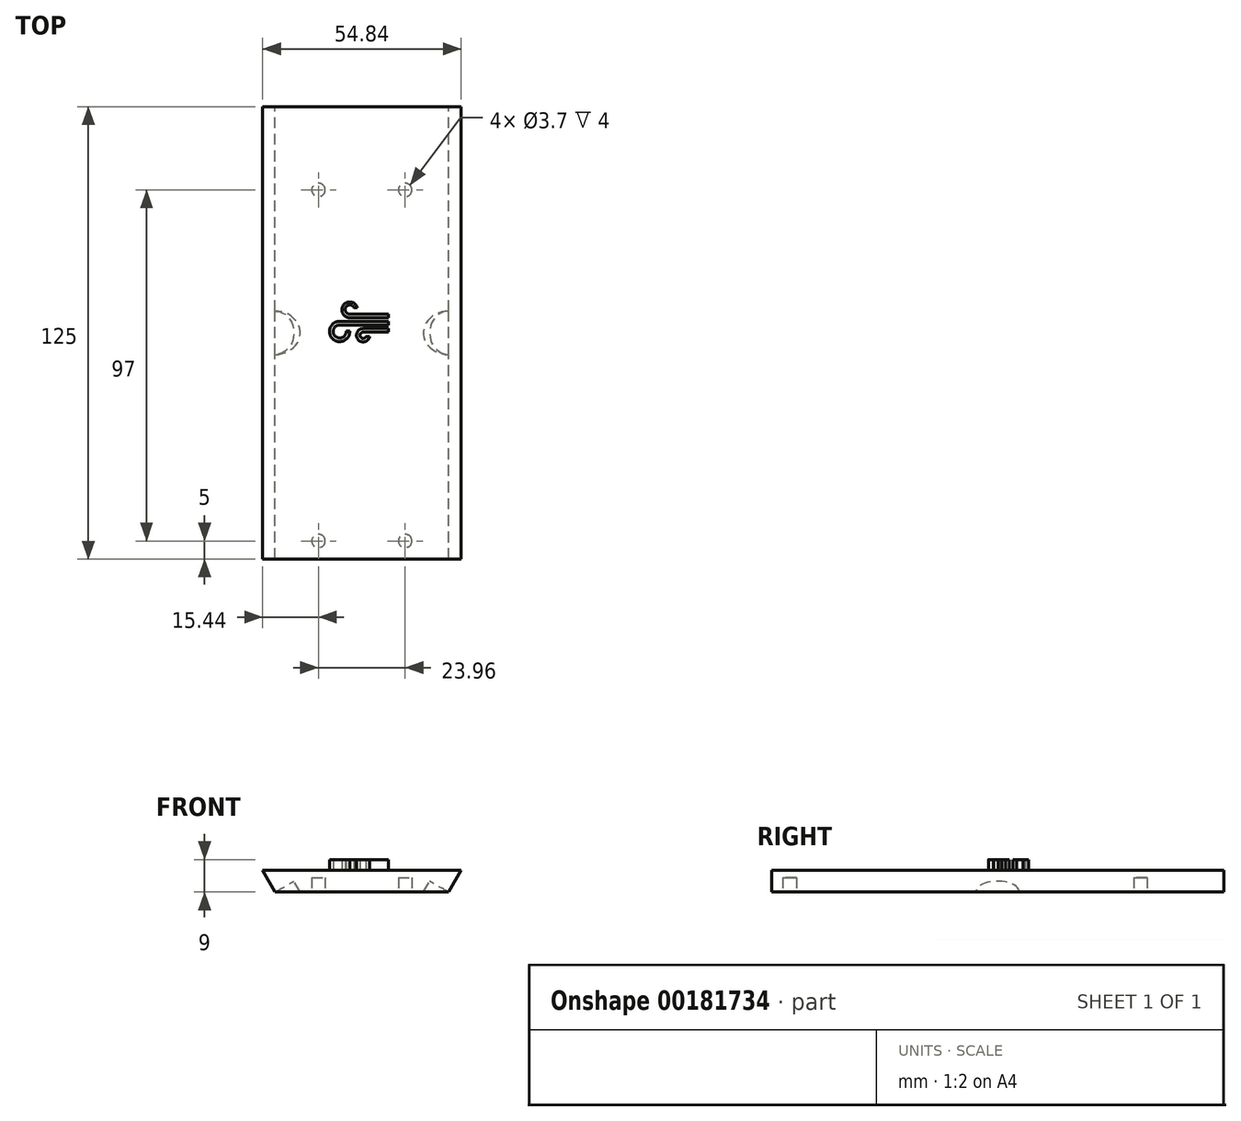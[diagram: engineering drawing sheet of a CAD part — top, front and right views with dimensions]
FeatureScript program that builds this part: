
annotation { "Feature Type Name" : "Feature", "Feature Type Description" : "" }
export const myFeature = defineFeature(function(context is Context, id is Id, definition is map)
    precondition{}
    {
        {
            var Q0;
            Q0=qCreatedBy(makeId("Front.planeOp"),FACE);
            var sketch = newSketch(context, id + "F0", { "sketchPlane" : qUnion([Q0])});
            skCircle(sketch, "E0.cCircle", {"center": v(0, 0) * mm, "radius": 47.5 * mm, "construction": true});
            skLineSegment(sketch, "E0.0", {"start": v(-27.42, -47.5) * mm, "end": v(-54.85, 0) * mm});
            skLineSegment(sketch, "E0.1", {"start": v(-54.85, 0) * mm, "end": v(-27.42, 47.5) * mm});
            skLineSegment(sketch, "E0.2", {"start": v(-27.42, 47.5) * mm, "end": v(27.42, 47.5) * mm});
            skLineSegment(sketch, "E0.3", {"start": v(27.42, 47.5) * mm, "end": v(54.85, 0) * mm});
            skLineSegment(sketch, "E0.4", {"start": v(54.85, 0) * mm, "end": v(27.42, -47.5) * mm});
            skLineSegment(sketch, "E0.5", {"start": v(27.42, -47.5) * mm, "end": v(-27.42, -47.5) * mm});
            skPoint(sketch, "E0.0.midPoint", {"position": v(-41.14, -23.75) * mm});
            skCircle(sketch, "E1.cCircle", {"center": v(0, 0) * mm, "radius": 41.5 * mm, "construction": true});
            skLineSegment(sketch, "E1.0", {"start": v(-23.96, -41.5) * mm, "end": v(-47.92, 0) * mm});
            skLineSegment(sketch, "E1.1", {"start": v(-47.92, 0) * mm, "end": v(-23.96, 41.5) * mm});
            skLineSegment(sketch, "E1.2", {"start": v(-23.96, 41.5) * mm, "end": v(23.96, 41.5) * mm});
            skLineSegment(sketch, "E1.3", {"start": v(23.96, 41.5) * mm, "end": v(47.92, 0) * mm});
            skLineSegment(sketch, "E1.4", {"start": v(47.92, 0) * mm, "end": v(23.96, -41.5) * mm});
            skLineSegment(sketch, "E1.5", {"start": v(23.96, -41.5) * mm, "end": v(-23.96, -41.5) * mm});
            skPoint(sketch, "E1.0.midPoint", {"position": v(-35.94, -20.75) * mm});
            skLineSegment(sketch, "E2", {"start": v(27.42, 47.5) * mm, "end": v(23.96, 41.5) * mm});
            skLineSegment(sketch, "E3", {"start": v(-27.42, 47.5) * mm, "end": v(-23.96, 41.5) * mm});
            skSolve(sketch);
        }
        {
            var Q0;
            Q0=makeQuery(id+"F0.imprint","IMPRINT",FACE,{"disambiguationData":[TD([[makeQuery(id+"F0.imprint","IMPRINT",EDGE,{"derivedFrom":sQuery(id+"F0.wireOp",EDGE,"E0.2")}),-1.0]])]});
            extrude(context, id + "F1", {"entities" : qUnion([Q0]), "depth" : 125 * mm});
        }
        {
            var Q0;
            Q0=makeQuery(id+"F1.opExtrude","SWEPT_FACE",FACE,{"disambiguationData":[OSD([sQuery(id+"F0.wireOp",EDGE,"E1.2")])]});
            var sketch = newSketch(context, id + "F2", { "sketchPlane" : qUnion([Q0])});
            skPoint(sketch, "E4", {"position": v(0, 125) * mm});
            skPoint(sketch, "E5", {"position": v(0, 120) * mm});
            skLineSegment(sketch, "E6", {"start": v(0, 120) * mm, "end": v(-23.96, 120) * mm});
            skPoint(sketch, "E7", {"position": v(-11.98, 120) * mm});
            skCircle(sketch, "E8", {"center": v(-11.98, 120) * mm, "radius": 1.85 * mm});
            skCircle(sketch, "E9.MirrorC", {"center": v(11.98, 120) * mm, "radius": 1.85 * mm});
            skPoint(sketch, "E10", {"position": v(0, 23) * mm});
            skLineSegment(sketch, "E11", {"start": v(0, 23) * mm, "end": v(-23.96, 23) * mm});
            skPoint(sketch, "E12", {"position": v(-11.98, 23) * mm});
            skCircle(sketch, "E13", {"center": v(-11.98, 23) * mm, "radius": 1.85 * mm});
            skCircle(sketch, "E14.MirrorC", {"center": v(11.98, 23) * mm, "radius": 1.85 * mm});
            skSolve(sketch);
        }
        {
            var Q0;
            Q0=qSketchRegion(id+"F2",true);
            extrude(context, id + "F3", {"entities" : qUnion([Q0]), "operationType" : NewBodyOperationType.REMOVE, "oppositeDirection" : true, "depth" : 4 * mm});
        }
        {
            var Q0;
            Q0=makeQuery(id+"F1.opExtrude","SWEPT_FACE",FACE,{"disambiguationData":[OSD([sQuery(id+"F0.wireOp",EDGE,"E0.2")])]});
            var sketch = newSketch(context, id + "F4", { "sketchPlane" : qUnion([Q0])});
            skPoint(sketch, "E15", {"position": v(-23.96, -62.5) * mm});
            skPoint(sketch, "E16", {"position": v(0, -90) * mm});
            skPoint(sketch, "E17", {"position": v(0, -62.5) * mm});
            skLineSegment(sketch, "E18.MirrorCS", {"start": v(0.37, -62.31) * mm, "end": v(0.37, -61.31) * mm});
            skArc(sketch, "E19.MirrorCS", {"start": v(0.37, -62.31) * mm, "mid": v(-0.37, -63.6) * mm, "end": v(1.11, -63.58) * mm});
            skArc(sketch, "E20.MirrorCS", {"start": v(0.37, -61.31) * mm, "mid": v(-1.08, -64.32) * mm, "end": v(2.17, -63.58) * mm});
            skLineSegment(sketch, "E21.MirrorCS", {"start": v(2.17, -63.58) * mm, "end": v(1.11, -63.58) * mm});
            skLineSegment(sketch, "E22.MirrorCS", {"start": v(7.37, -60.31) * mm, "end": v(7.37, -59.31) * mm});
            skLineSegment(sketch, "E23.MirrorCS", {"start": v(7.37, -62.31) * mm, "end": v(7.37, -61.31) * mm});
            skArc(sketch, "E24.MirrorCS", {"start": v(-2.2, -55.52) * mm, "mid": v(-4.4, -55.37) * mm, "end": v(-3.33, -57.31) * mm});
            skLineSegment(sketch, "E25.MirrorCS", {"start": v(-3.33, -58.31) * mm, "end": v(-3.33, -57.31) * mm});
            skLineSegment(sketch, "E26.MirrorCS", {"start": v(-1.25, -55.52) * mm, "end": v(-2.2, -55.52) * mm});
            skLineSegment(sketch, "E27.MirrorCS", {"start": v(-6.13, -60.31) * mm, "end": v(-6.13, -59.31) * mm});
            skLineSegment(sketch, "E28.MirrorCS", {"start": v(7.34, -58.31) * mm, "end": v(7.34, -57.31) * mm});
            skLineSegment(sketch, "E29.MirrorCS", {"start": v(-3.33, -62) * mm, "end": v(-4.33, -62) * mm});
            skArc(sketch, "E30.MirrorCS", {"start": v(-1.25, -55.52) * mm, "mid": v(-5.08, -54.83) * mm, "end": v(-3.33, -58.31) * mm});
            skLineSegment(sketch, "E31.MirrorCS", {"start": v(7.37, -62.31) * mm, "end": v(0.37, -62.31) * mm});
            skArc(sketch, "E32.MirrorCS", {"start": v(-6.13, -60.31) * mm, "mid": v(-7.37, -63.43) * mm, "end": v(-4.33, -62) * mm});
            skLineSegment(sketch, "E33.MirrorCS", {"start": v(7.37, -61.31) * mm, "end": v(0.37, -61.31) * mm});
            skLineSegment(sketch, "E34.MirrorCS", {"start": v(7.37, -60.31) * mm, "end": v(-6.13, -60.31) * mm});
            skArc(sketch, "E35.MirrorCS", {"start": v(-6.13, -59.31) * mm, "mid": v(-8.07, -64.14) * mm, "end": v(-3.33, -62) * mm});
            skPoint(sketch, "E36.MirrorP", {"position": v(-1.73, -50.22) * mm});
            skLineSegment(sketch, "E37.MirrorCS", {"start": v(7.37, -59.31) * mm, "end": v(-6.13, -59.31) * mm});
            skLineSegment(sketch, "E38.MirrorCS", {"start": v(-11.73, -70.22) * mm, "end": v(-11.73, -50.22) * mm});
            skLineSegment(sketch, "E39.MirrorCS", {"start": v(8.27, -50.22) * mm, "end": v(-11.73, -50.22) * mm});
            skLineSegment(sketch, "E40.MirrorCS", {"start": v(7.34, -58.31) * mm, "end": v(-3.33, -58.31) * mm});
            skLineSegment(sketch, "E41.MirrorCS", {"start": v(7.34, -57.31) * mm, "end": v(-3.33, -57.31) * mm});
            skLineSegment(sketch, "E42.MirrorCS", {"start": v(8.27, -70.22) * mm, "end": v(8.27, -50.22) * mm});
            skLineSegment(sketch, "E43.MirrorCS", {"start": v(8.27, -70.22) * mm, "end": v(-11.73, -70.22) * mm});
            skSolve(sketch);
        }
        {
            var Q0;
            Q0=makeQuery(id+"F4.imprint","IMPRINT",FACE,{"disambiguationData":[TD([[makeQuery(id+"F4.imprint","IMPRINT",EDGE,{"derivedFrom":sQuery(id+"F4.wireOp",EDGE,"E18.MirrorCS")}),-1.0]])]});
            var Q1;
            Q1=makeQuery(id+"F4.imprint","IMPRINT",FACE,{"disambiguationData":[TD([[makeQuery(id+"F4.imprint","IMPRINT",EDGE,{"derivedFrom":sQuery(id+"F4.wireOp",EDGE,"E18.MirrorCS")}),1.0]])]});
            var Q2;
            Q2=makeQuery(id+"F4.imprint","IMPRINT",FACE,{"disambiguationData":[TD([[makeQuery(id+"F4.imprint","IMPRINT",EDGE,{"derivedFrom":sQuery(id+"F4.wireOp",EDGE,"E27.MirrorCS")}),1.0]])]});
            var Q3;
            Q3=makeQuery(id+"F4.imprint","IMPRINT",FACE,{"disambiguationData":[TD([[makeQuery(id+"F4.imprint","IMPRINT",EDGE,{"derivedFrom":sQuery(id+"F4.wireOp",EDGE,"E22.MirrorCS")}),1.0]])]});
            var Q4;
            Q4=makeQuery(id+"F4.imprint","IMPRINT",FACE,{"disambiguationData":[TD([[makeQuery(id+"F4.imprint","IMPRINT",EDGE,{"derivedFrom":sQuery(id+"F4.wireOp",EDGE,"E25.MirrorCS")}),-1.0]])]});
            var Q5;
            Q5=makeQuery(id+"F4.imprint","IMPRINT",FACE,{"disambiguationData":[TD([[makeQuery(id+"F4.imprint","IMPRINT",EDGE,{"derivedFrom":sQuery(id+"F4.wireOp",EDGE,"E24.MirrorCS")}),-1.0]])]});
            extrude(context, id + "F5", {"entities" : qUnion([Q0, Q1, Q2, Q3, Q4, Q5]), "operationType" : NewBodyOperationType.ADD, "depth" : 3 * mm});
        }
        {
            var Q0;
            Q0=makeQuery(id+"F1.opExtrude","SWEPT_EDGE",EDGE,{"disambiguationData":[OSD([sQuery(id+"F0.wireOp",EDGE,"E1.1"),sQuery(id+"F0.wireOp",EDGE,"E1.2"),sQuery(id+"F0.wireOp",EDGE,"E3")])]});
            cPlane(context, id + "F6", {"entities" : qUnion([Q0]), "cplaneType" : CPlaneType.LINE_ANGLE, "offset" : 25 * mm, "angle" : 150 * degree, "width" : 150 * mm, "height" : 150 * mm});
        }
        {
            var Q0;
            Q0=qCreatedBy(id+"F6.planeOp",FACE);
            var sketch = newSketch(context, id + "F7", { "sketchPlane" : qUnion([Q0])});
            skCircle(sketch, "E44", {"center": v(0, 62.5) * mm, "radius": 6 * mm});
            skSolve(sketch);
        }
        {
            var Q0;
            Q0=qSketchRegion(id+"F7",true);
            extrude(context, id + "F8", {"entities" : qUnion([Q0]), "operationType" : NewBodyOperationType.REMOVE, "depth" : 25 * mm});
        }
        {
            var Q0;
            Q0=makeQuery(id+"F1.opExtrude","SWEPT_EDGE",EDGE,{"disambiguationData":[OSD([sQuery(id+"F0.wireOp",EDGE,"E1.2"),sQuery(id+"F0.wireOp",EDGE,"E1.3"),sQuery(id+"F0.wireOp",EDGE,"E2")])]});
            cPlane(context, id + "F9", {"entities" : qUnion([Q0]), "cplaneType" : CPlaneType.LINE_ANGLE, "offset" : 25 * mm, "angle" : 30 * degree, "width" : 150 * mm, "height" : 150 * mm});
        }
        {
            var Q0;
            Q0=qCreatedBy(id+"F9.planeOp",FACE);
            var sketch = newSketch(context, id + "F10", { "sketchPlane" : qUnion([Q0])});
            skCircle(sketch, "E45", {"center": v(0, -62.5) * mm, "radius": 6 * mm});
            skSolve(sketch);
        }
        {
            var Q0;
            Q0=qSketchRegion(id+"F10",true);
            extrude(context, id + "F11", {"entities" : qUnion([Q0]), "operationType" : NewBodyOperationType.REMOVE, "oppositeDirection" : true, "depth" : 25 * mm});
        }
    });
